# Revit family: BE_84000_de_DE
name_source: partatom
category: Leuchten
revit_build: Autodesk Revit 2015 (Build: 20160512_0715(x64)
units: mm (PartAtom-declared; Revit-internal decimal feet)

## types (2) — shared parameters
Aktualisierung = 2017-01-27T04:13:58
BEGA_Dummy = Nein
BEGA_IES = Ja
BEGA_Intern = Ja
BEGA_Intern_Konstruktion = Ja
BEGA_Intern_an = Ja
BEGA_Intern_aus = Ja
Beschreibung = Pollerleuchtenrohr
Beschreibung_Sonderanfertigung = Hier können Sie Informationen zur Sonderanfertigung eintragen.
Bestellnummer_Erdstück = ---
CE_Konformität = ja
Erdstück = Nein
Gewicht = 3.15 kg
Hersteller = BEGA
Lastklassifizierung = Beleuchtung
Logo = BEGA_Logo.png
M_W = Nein
Material_02 = BEGA_Oberfläche_Silber_matt
Material_03 = BEGA_Oberfläche_Weiss_matt
Material_06 = BEGA_Oberfläche_Edelstahl_gebürstet
Material_09 = BEGA_Glas_klar
Material_11 = BEGA_Glas_opal
Material_17 = BEGA_Reflektor
Material_18 = BEGA_Gummi_schwarz
Produktdatenblatt = http://www.bega.de
Scheinlast = 0 VA
Sonderanfertigung = Nein
Typenbild = 84000.png
URL = http://www.bega.de
zero-valued in all types: Vorgabe-Ansicht

## per-type parameters (varying)
| type | Bestellnummer | M_A | M_G | Modell |
| BEGA_84000_Grafit | 84000 | Nein | Ja | 84000 |
| BEGA_84000_Silber | 84000A | Ja | Nein | 84000A |
